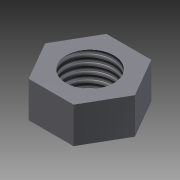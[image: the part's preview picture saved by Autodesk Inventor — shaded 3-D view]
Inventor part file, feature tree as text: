
AUTODESK INVENTOR PART (.ipt)
format: ipt  version: 2012 (Build 160160000, 160)  size: 82,944 bytes
history: native  units: mm
features: extrude x1, thread x1, sketch x1
ambient origin geometry x8: Origin, YZ Plane, XZ Plane, XY Plane, X Axis, Y Axis, Z Axis, Center Point
bodies: Solid1 (feature_tree)
feature tree (3):
  extrude  "Extrusion1"  Depth=13.0mm
  thread  "Thread1"  [1 undecoded]
  sketch  "Sketch1"  dims[d0=8.0mm d2=13.0mm d3=6.0mm d4=0.0mm d5=10.0mm d6=0.0mm]
note: 1 required parameter value undecoded (feature->parameter linkage not recoverable at this tier; creation-order binding heuristic only, values carry confidence <= 0.55)
